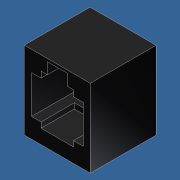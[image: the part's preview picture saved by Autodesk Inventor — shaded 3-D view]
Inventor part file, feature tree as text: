
AUTODESK INVENTOR PART (.ipt)
format: ipt  version: 2012 (Build 160160000, 160)  size: 327,168 bytes
history: native  units: in
note: dims shown in document units (in); Inventor stores cm internally (conversion verified against a paired STEP export)
features: extrude x7, sketch x7, fillet x1
ambient origin geometry x8: Origin, YZ Plane, XZ Plane, XY Plane, X Axis, Y Axis, Z Axis, Center Point
bodies: Solid1 (feature_tree)
feature tree (15):
  extrude  "Extrusion1"  Depth=0.62in
  extrude  "Extrusion2"  Depth=0.022in
  extrude  "Extrusion3"  Depth=0.184in
  extrude  "Extrusion4"  Depth=0.05in
  extrude  "Extrusion5"  Depth=0.048in
  fillet  "Fillet1"  Radius=0.258in
  extrude  "Extrusion6"  Depth=0.076in
  extrude  "Extrusion7"  Depth=0.303in
  sketch  "Sketch1"  dims[d0=0.526in d1=0.62in]
  sketch  "Sketch2"  dims[d2=0.524in d3=0.0in d4=0.022in]
  sketch  "Sketch3"  dims[d5=0.184in d6=0.184in]
  sketch  "Sketch4"  dims[d7=0.09in d9=0.05in]
  sketch  "Sketch5"  dims[d10=0.05in d11=0.048in d13=0.258in]
  sketch  "Sketch6"  dims[d14=0.076in d15=0.076in]
  sketch  "Sketch7"  dims[d16=0.41in d17=0.303in d18=0.076in d19=0.076in d20=0.043in d21=0.114in d22=0.557in d23=0.0in d24=0.005in d25=0.0in d26=0.01in d27=0.01in d28=0.01in d29=0.01in d30=0.015in d31=0.015in d32=0.015in d33=0.0865in d34=0.0865in d35=0.254in d36=0.0in d37=0.15in d38=0.0in d39=0.005in d40=0.043in d41=0.043in d42=0.0in d43=0.0in d44=0.0in d45=0.0in d46=0.087in d47=0.087in d48=0.254in d49=0.0in d50=5.0in d51=0.0in]
